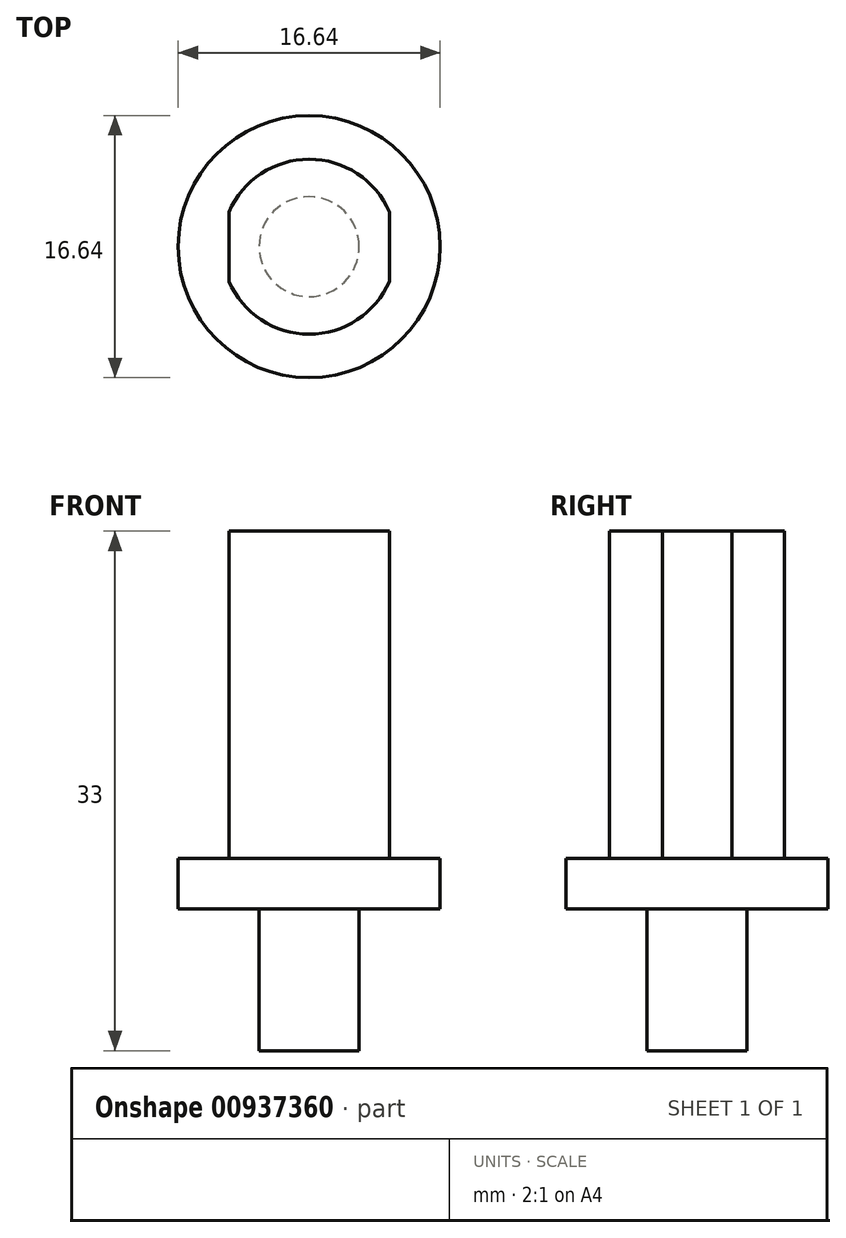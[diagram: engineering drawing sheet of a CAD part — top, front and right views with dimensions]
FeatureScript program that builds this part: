
annotation { "Feature Type Name" : "Feature", "Feature Type Description" : "" }
export const myFeature = defineFeature(function(context is Context, id is Id, definition is map)
    precondition{}
    {
        {
            var Q0;
            Q0=qCreatedBy(makeId("Top.planeOp"),FACE);
            var sketch = newSketch(context, id + "F0", { "sketchPlane" : qUnion([Q0])});
            skCircle(sketch, "E0", {"center": v(0, 0) * mm, "radius": 8.32 * mm});
            skSolve(sketch);
        }
        {
            var Q0;
            Q0 = qSketchRegion(id + "F0", true);
            extrude(context, id + "F1", {"entities" : qUnion([Q0]), "depth" : 3.2 * mm, "offsetDistance" : 25.4 * mm});
        }
        {
            var Q0;
            Q0=makeQuery(id+"F1.opExtrude","CAP_FACE",FACE,{"disambiguationData":[OSD([sQuery(id+"F0.wireOp",EDGE,"E0")])],"isStart":false});
            var sketch = newSketch(context, id + "F2", { "sketchPlane" : qUnion([Q0])});
            skCircle(sketch, "E1", {"center": v(0, 0) * mm, "radius": 5.56 * mm});
            skLineSegment(sketch, "E2", {"start": v(-5.1, 2.2) * mm, "end": v(-5.1, -2.2) * mm});
            skLineSegment(sketch, "E3", {"start": v(5.1, 2.2) * mm, "end": v(5.1, -2.2) * mm});
            skSolve(sketch);
        }
        {
            var Q0;
            {var subQ0=sQuery(id+"F2.wireOp",EDGE,"E2");Q0=makeQuery(id+"F2.imprint","IMPRINT",FACE,{"disambiguationData":[TD([[makeQuery(id+"F2.imprint","IMPRINT",EDGE,{"derivedFrom":subQ0}),1.0]])]});}
            extrude(context, id + "F3", {"entities" : qUnion([Q0]), "operationType" : NewBodyOperationType.ADD, "depth" : 20.8 * mm, "offsetDistance" : 25.4 * mm});
        }
        {
            var Q0;
            Q0=makeQuery(id+"F1.opExtrude","CAP_FACE",FACE,{"disambiguationData":[OSD([sQuery(id+"F0.wireOp",EDGE,"E0")])],"isStart":true});
            var sketch = newSketch(context, id + "F4", { "sketchPlane" : qUnion([Q0])});
            skCircle(sketch, "E4", {"center": v(0, 0) * mm, "radius": 3.18 * mm});
            skSolve(sketch);
        }
        {
            var Q0;
            Q0=makeQuery(id+"F4.imprint","IMPRINT",FACE,{"disambiguationData":[TD([[makeQuery(id+"F4.imprint","IMPRINT",EDGE,{"derivedFrom":sQuery(id+"F4.wireOp",EDGE,"E4")}),1.0]])]});
            extrude(context, id + "F5", {"entities" : qUnion([Q0]), "operationType" : NewBodyOperationType.ADD, "depth" : 9 * mm, "offsetDistance" : 25.4 * mm});
        }
    });
